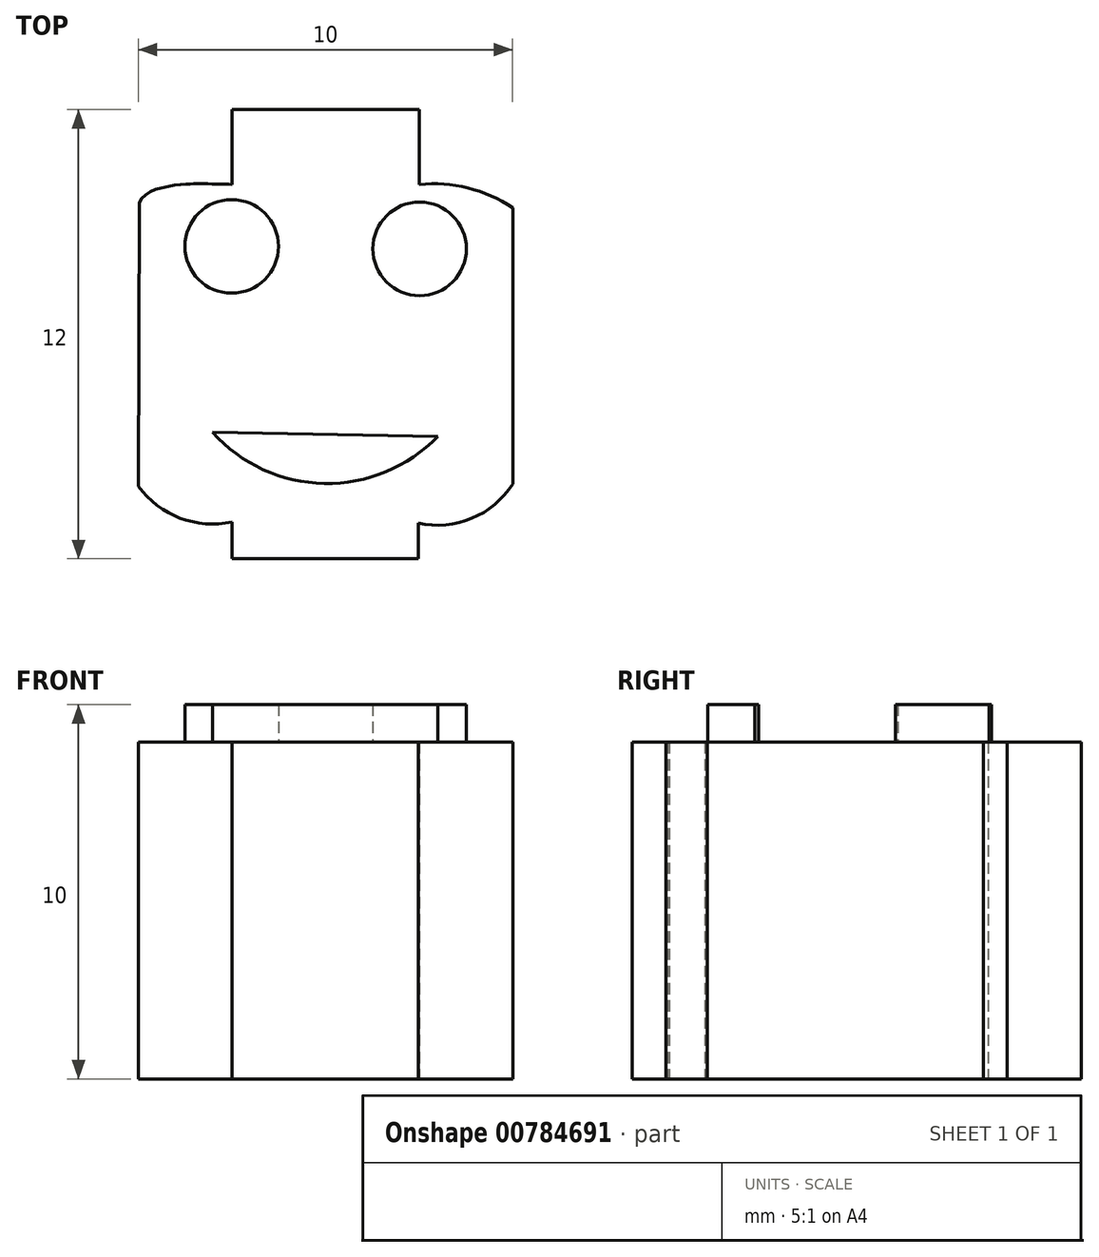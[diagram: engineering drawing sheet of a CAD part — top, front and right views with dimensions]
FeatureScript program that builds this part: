
annotation { "Feature Type Name" : "Feature", "Feature Type Description" : "" }
export const myFeature = defineFeature(function(context is Context, id is Id, definition is map)
    precondition{}
    {
        {
            var Q0;
            Q0=qCreatedBy(makeId("Top.planeOp"),FACE);
            var sketch = newSketch(context, id + "F0", { "sketchPlane" : qUnion([Q0])});
            skLineSegment(sketch, "E0", {"start": v(-34.49, 0) * mm, "end": v(-20.49, 0) * mm});
            skLineSegment(sketch, "E1", {"start": v(-20.49, 0) * mm, "end": v(-20.49, -12) * mm});
            skLineSegment(sketch, "E2", {"start": v(-20.49, -12) * mm, "end": v(-34.49, -12) * mm});
            skLineSegment(sketch, "E3", {"start": v(-34.49, -12) * mm, "end": v(-34.49, 0) * mm});
            skLineSegment(sketch, "E4", {"start": v(-27.49, -12) * mm, "end": v(-22.49, -12) * mm});
            skLineSegment(sketch, "E5", {"start": v(-22.49, -12) * mm, "end": v(-32.49, -12) * mm});
            skLineSegment(sketch, "E6", {"start": v(-32.49, -12) * mm, "end": v(-32.49, 0) * mm});
            skLineSegment(sketch, "E7", {"start": v(-22.49, -12) * mm, "end": v(-22.49, 0) * mm});
            skLineSegment(sketch, "E8", {"start": v(-27.49, 0) * mm, "end": v(-24.99, 0) * mm});
            skLineSegment(sketch, "E9", {"start": v(-24.99, 0) * mm, "end": v(-29.99, 0) * mm});
            skLineSegment(sketch, "E10", {"start": v(-29.99, 0) * mm, "end": v(-29.99, -2) * mm});
            skLineSegment(sketch, "E11", {"start": v(-24.99, 0) * mm, "end": v(-24.99, -2) * mm});
            skFitSpline(sketch, "E12", {"points": [v(-29.99, -2) * mm, v(-30.82, -1.98) * mm, v(-31.07, -1.98) * mm, v(-32.49, -2.6) * mm], "startDerivative": vector(-1.81, 0.17) * mm, "endDerivative": vector(-0.13, -3.4) * mm});
            skLineSegment(sketch, "E13", {"start": v(-32.47, -2.07) * mm, "end": v(-32.49, -10.07) * mm});
            skPoint(sketch, "E14", {"position": v(-24.99, -2) * mm});
            skPoint(sketch, "E15.1.internal.orphan", {"position": v(-24.52, -2) * mm});
            skPoint(sketch, "E15.2.internal.orphan", {"position": v(-22.49, -2) * mm});
            skPoint(sketch, "E16", {"position": v(-23.86, -1.96) * mm});
            skPoint(sketch, "E17", {"position": v(-23.22, -1.96) * mm});
            skArc(sketch, "E18", {"start": v(-22.49, -2.62) * mm, "mid": v(-23.68, -2.1) * mm, "end": v(-24.99, -2) * mm});
            skLineSegment(sketch, "E19", {"start": v(-22.49, -2) * mm, "end": v(-22.49, -10) * mm});
            skLineSegment(sketch, "E20", {"start": v(-25.01, -12) * mm, "end": v(-30.26, -12) * mm});
            skLineSegment(sketch, "E21", {"start": v(-22.49, -12) * mm, "end": v(-29.99, -12) * mm});
            skLineSegment(sketch, "E22.trimOffspring", {"start": v(-30.26, -12) * mm, "end": v(-32.49, -12) * mm});
            skArc(sketch, "E23", {"start": v(-32.49, -10.07) * mm, "mid": v(-31.38, -10.91) * mm, "end": v(-29.99, -11.02) * mm});
            skArc(sketch, "E24", {"start": v(-25.01, -11.05) * mm, "mid": v(-23.58, -10.92) * mm, "end": v(-22.49, -10) * mm});
            skLineSegment(sketch, "E25.trimOffspring", {"start": v(-29.99, -11.02) * mm, "end": v(-29.99, -12) * mm});
            skLineSegment(sketch, "E26.trimOffspring", {"start": v(-25.01, -11.05) * mm, "end": v(-25.01, -12) * mm});
            skLineSegment(sketch, "E27", {"start": v(-29.99, -2) * mm, "end": v(-24.99, -2) * mm});
            skLineSegment(sketch, "E28", {"start": v(-29.99, -11.02) * mm, "end": v(-25.01, -11.05) * mm});
            skLineSegment(sketch, "E29", {"start": v(-25.01, -12) * mm, "end": v(-29.99, -12) * mm});
            skSolve(sketch);
        }
        {
            var Q0;
            {var subQ0=sQuery(id+"F0.wireOp",EDGE,"E18");Q0=makeQuery(id+"F0.imprint","IMPRINT",FACE,{"disambiguationData":[TD([[makeQuery(id+"F0.imprint","IMPRINT",EDGE,{"derivedFrom":subQ0}),1.0]])]});}
            var Q1;
            {var subQ3=sQuery(id+"F0.wireOp",EDGE,"E10");Q1=makeQuery(id+"F0.imprint","IMPRINT",FACE,{"disambiguationData":[TD([[makeQuery(id+"F0.imprint","IMPRINT",EDGE,{"derivedFrom":subQ3}),1.0]])]});}
            var Q2;
            {var subQ0=sQuery(id+"F0.wireOp",EDGE,"E25.trimOffspring");Q2=makeQuery(id+"F0.imprint","IMPRINT",FACE,{"disambiguationData":[TD([[makeQuery(id+"F0.imprint","IMPRINT",EDGE,{"derivedFrom":subQ0}),1.0]])]});}
            extrude(context, id + "F1", {"entities" : qUnion([Q0, Q1, Q2]), "depth" : 9 * mm, "offsetDistance" : 25 * mm});
        }
        {
            var Q0;
            Q0=makeQuery(id+"F1.opExtrude","CAP_FACE",FACE,{"disambiguationData":[OSD([sQuery(id+"F0.wireOp",EDGE,"E9"),sQuery(id+"F0.wireOp",EDGE,"E10"),sQuery(id+"F0.wireOp",EDGE,"E11"),sQuery(id+"F0.wireOp",EDGE,"E12"),sQuery(id+"F0.wireOp",EDGE,"E13"),sQuery(id+"F0.wireOp",EDGE,"E18"),sQuery(id+"F0.wireOp",EDGE,"E19"),sQuery(id+"F0.wireOp",EDGE,"E23"),sQuery(id+"F0.wireOp",EDGE,"E24"),sQuery(id+"F0.wireOp",EDGE,"E25.trimOffspring"),sQuery(id+"F0.wireOp",EDGE,"E26.trimOffspring"),sQuery(id+"F0.wireOp",EDGE,"E29")])],"isStart":false});
            var sketch = newSketch(context, id + "F2", { "sketchPlane" : qUnion([Q0])});
            skCircle(sketch, "E30", {"center": v(-30, -3.65) * mm, "radius": 1.25 * mm});
            skCircle(sketch, "E31", {"center": v(-24.98, -3.72) * mm, "radius": 1.25 * mm});
            skArc(sketch, "E32", {"start": v(-30.5, -8.63) * mm, "mid": v(-27.52, -9.99) * mm, "end": v(-24.5, -8.73) * mm});
            skLineSegment(sketch, "E33", {"start": v(-30.5, -8.63) * mm, "end": v(-24.5, -8.73) * mm});
            skSolve(sketch);
        }
        {
            var Q0;
            Q0=makeQuery(id+"F2.imprint","IMPRINT",FACE,{"disambiguationData":[TD([[makeQuery(id+"F2.imprint","IMPRINT",EDGE,{"derivedFrom":sQuery(id+"F2.wireOp",EDGE,"E30")}),1.0]])]});
            var Q1;
            Q1=makeQuery(id+"F2.imprint","IMPRINT",FACE,{"disambiguationData":[TD([[makeQuery(id+"F2.imprint","IMPRINT",EDGE,{"derivedFrom":sQuery(id+"F2.wireOp",EDGE,"E31")}),1.0]])]});
            var Q2;
            Q2=makeQuery(id+"F2.imprint","IMPRINT",FACE,{"disambiguationData":[TD([[makeQuery(id+"F2.imprint","IMPRINT",EDGE,{"derivedFrom":sQuery(id+"F2.wireOp",EDGE,"E32")}),1.0]])]});
            extrude(context, id + "F3", {"entities" : qUnion([Q0, Q1, Q2]), "operationType" : NewBodyOperationType.ADD, "depth" : 1 * mm, "offsetDistance" : 25 * mm});
        }
        {
            var Q0;
            Q0=makeQuery(id+"F3.opExtrude","CAP_FACE",FACE,{"disambiguationData":[OSD([sQuery(id+"F2.wireOp",EDGE,"E30")])],"isStart":false});
            var sketch = newSketch(context, id + "F4", { "sketchPlane" : qUnion([Q0])});
            skCircle(sketch, "E34", {"center": v(-30, -3.65) * mm, "radius": 0.62 * mm});
            skSolve(sketch);
        }
        {
            var Q0;
            Q0=makeQuery(id+"F3.opExtrude","CAP_FACE",FACE,{"disambiguationData":[OSD([sQuery(id+"F2.wireOp",EDGE,"E31")])],"isStart":false});
            var sketch = newSketch(context, id + "F5", { "sketchPlane" : qUnion([Q0])});
            skCircle(sketch, "E35", {"center": v(-24.98, -3.72) * mm, "radius": 0.62 * mm});
            skSolve(sketch);
        }
        {
            var Q0;
            Q0=makeQuery(id+"F4.imprint","IMPRINT",FACE,{"disambiguationData":[TD([[makeQuery(id+"F4.imprint","IMPRINT",EDGE,{"derivedFrom":sQuery(id+"F4.wireOp",EDGE,"E34")}),1.0]])]});
            var Q1;
            Q1=makeQuery(id+"F5.imprint","IMPRINT",FACE,{"disambiguationData":[TD([[makeQuery(id+"F5.imprint","IMPRINT",EDGE,{"derivedFrom":sQuery(id+"F5.wireOp",EDGE,"E35")}),1.0]])]});
            extrude(context, id + "F6", {"entities" : qUnion([Q0, Q1]), "operationType" : NewBodyOperationType.REMOVE, "depth" : 1 * mm, "offsetDistance" : 25 * mm});
        }
    });
